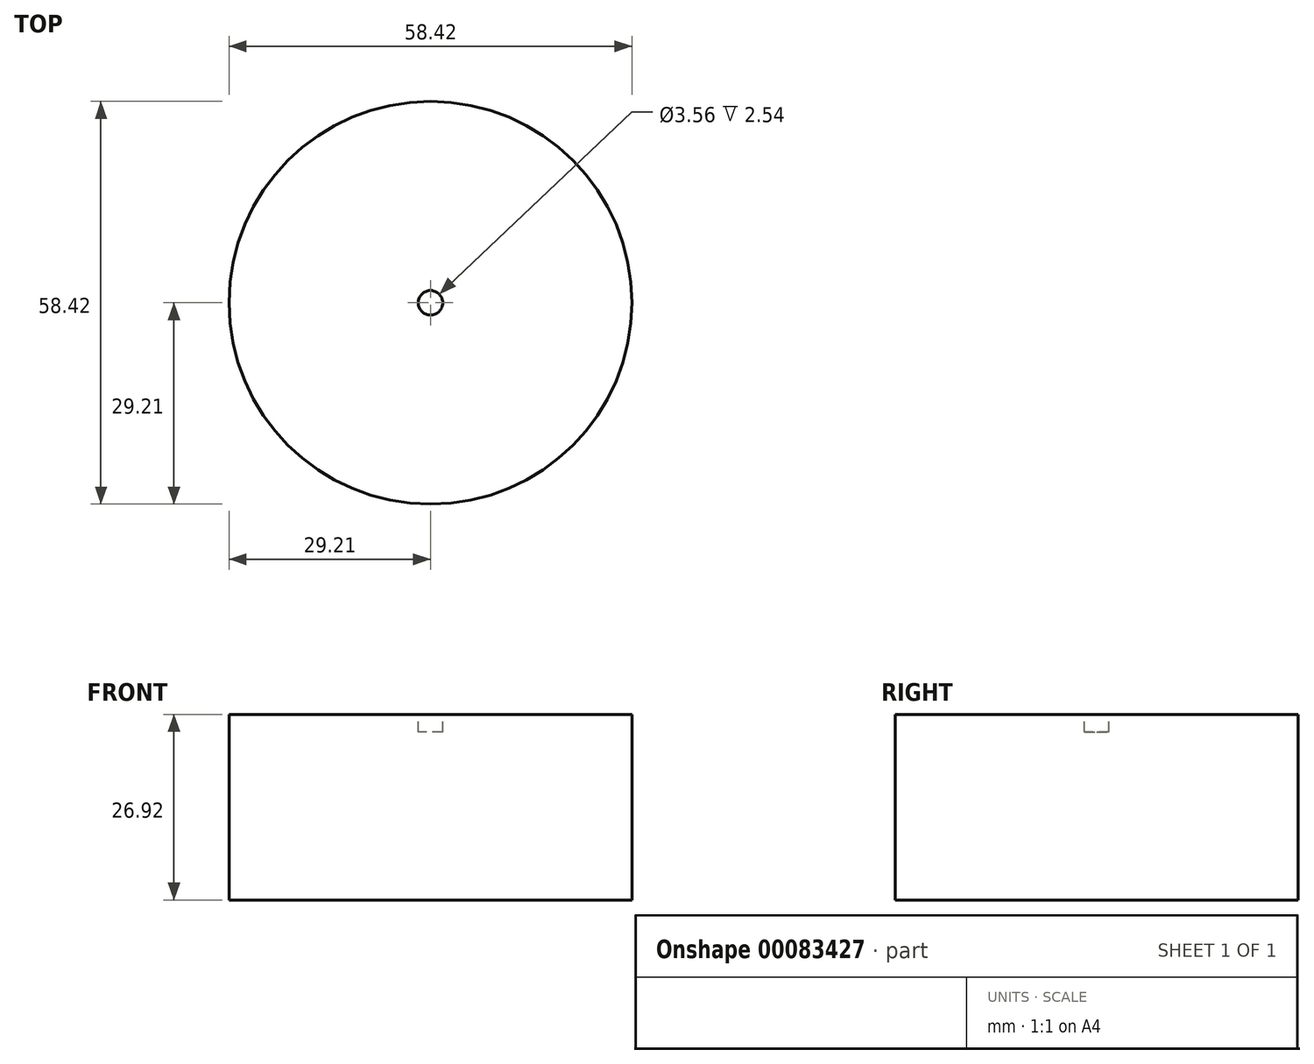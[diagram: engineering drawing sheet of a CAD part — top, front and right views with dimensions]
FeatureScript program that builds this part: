
annotation { "Feature Type Name" : "Feature", "Feature Type Description" : "" }
export const myFeature = defineFeature(function(context is Context, id is Id, definition is map)
    precondition{}
    {
        {
            var Q0;
            Q0=qCreatedBy(makeId("Top.planeOp"),FACE);
            var sketch = newSketch(context, id + "F0", { "sketchPlane" : qUnion([Q0])});
            skCircle(sketch, "E0", {"center": v(0, 0) * mm, "radius": 29.21 * mm});
            skSolve(sketch);
        }
        {
            var Q0;
            Q0 = qSketchRegion(id + "F0", true);
            extrude(context, id + "F1", {"entities" : qUnion([Q0]), "endBound" : BoundingType.SYMMETRIC, "depth" : 26.92 * mm});
        }
        {
            var Q0;
            Q0=makeQuery(id+"F1.opExtrude","CAP_FACE",FACE,{"disambiguationData":[OSD([sQuery(id+"F0.wireOp",EDGE,"E0")])],"isStart":false});
            var sketch = newSketch(context, id + "F2", { "sketchPlane" : qUnion([Q0])});
            skCircle(sketch, "E1", {"center": v(0, 0) * mm, "radius": 1.78 * mm});
            skSolve(sketch);
        }
        {
            var Q0;
            Q0 = qSketchRegion(id + "F2", true);
            extrude(context, id + "F3", {"entities" : qUnion([Q0]), "operationType" : NewBodyOperationType.REMOVE, "oppositeDirection" : true, "depth" : 2.54 * mm});
        }
    });
